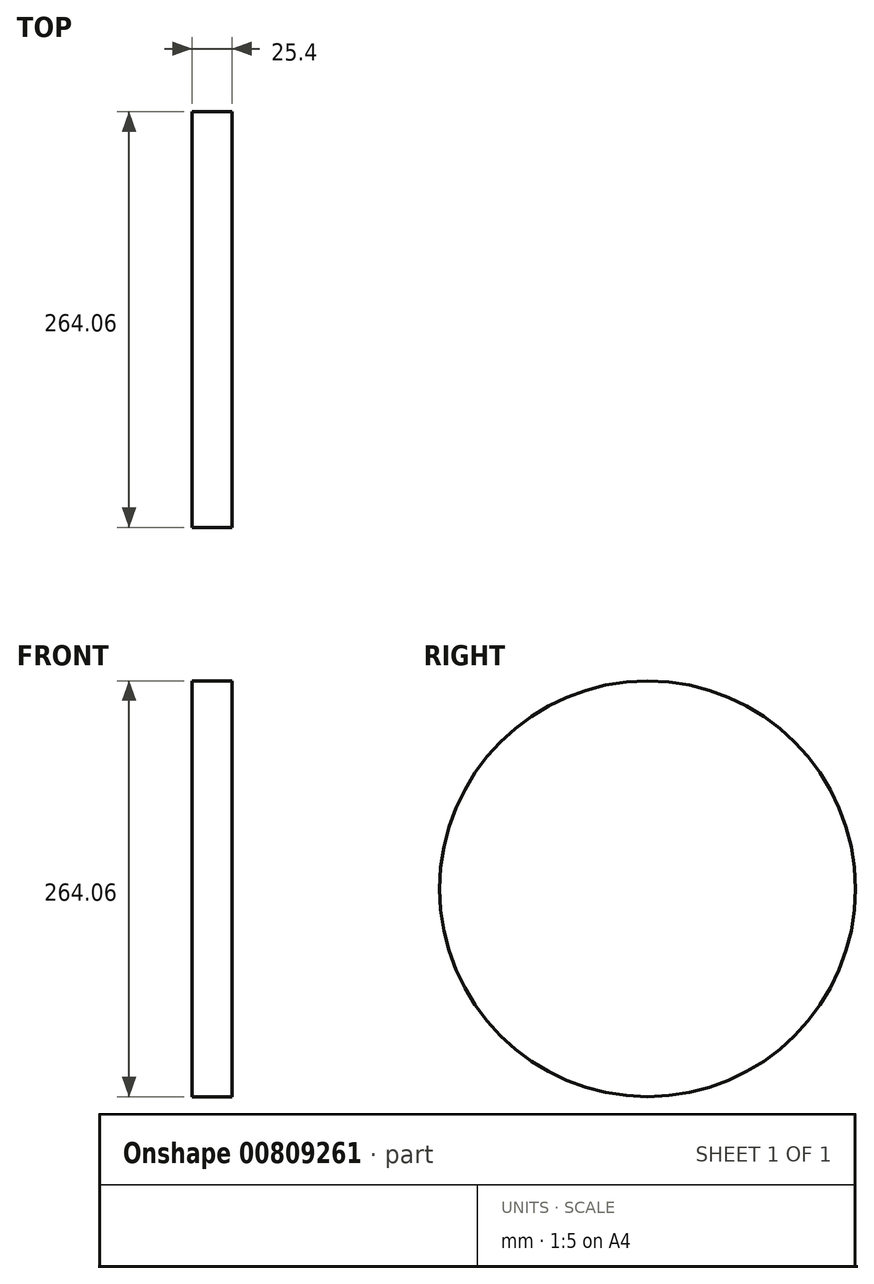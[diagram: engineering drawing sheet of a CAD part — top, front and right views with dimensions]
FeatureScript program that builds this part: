
annotation { "Feature Type Name" : "Feature", "Feature Type Description" : "" }
export const myFeature = defineFeature(function(context is Context, id is Id, definition is map)
    precondition{}
    {
        {
            var Q0;
            Q0=qCreatedBy(makeId("Right.planeOp"),FACE);
            var sketch = newSketch(context, id + "F0", { "sketchPlane" : qUnion([Q0])});
            skCircle(sketch, "E0", {"center": v(0, 0) * mm, "radius": 132.03 * mm});
            skSolve(sketch);
        }
        {
            var Q0;
            Q0=makeQuery(id+"F0.imprint","IMPRINT",FACE,{"disambiguationData":[TD([[makeQuery(id+"F0.imprint","IMPRINT",EDGE,{"derivedFrom":sQuery(id+"F0.wireOp",EDGE,"E0")}),1.0]])]});
            extrude(context, id + "F1", {"entities" : qUnion([Q0]), "depth" : 25.4 * mm, "offsetDistance" : 25.4 * mm});
        }
    });
